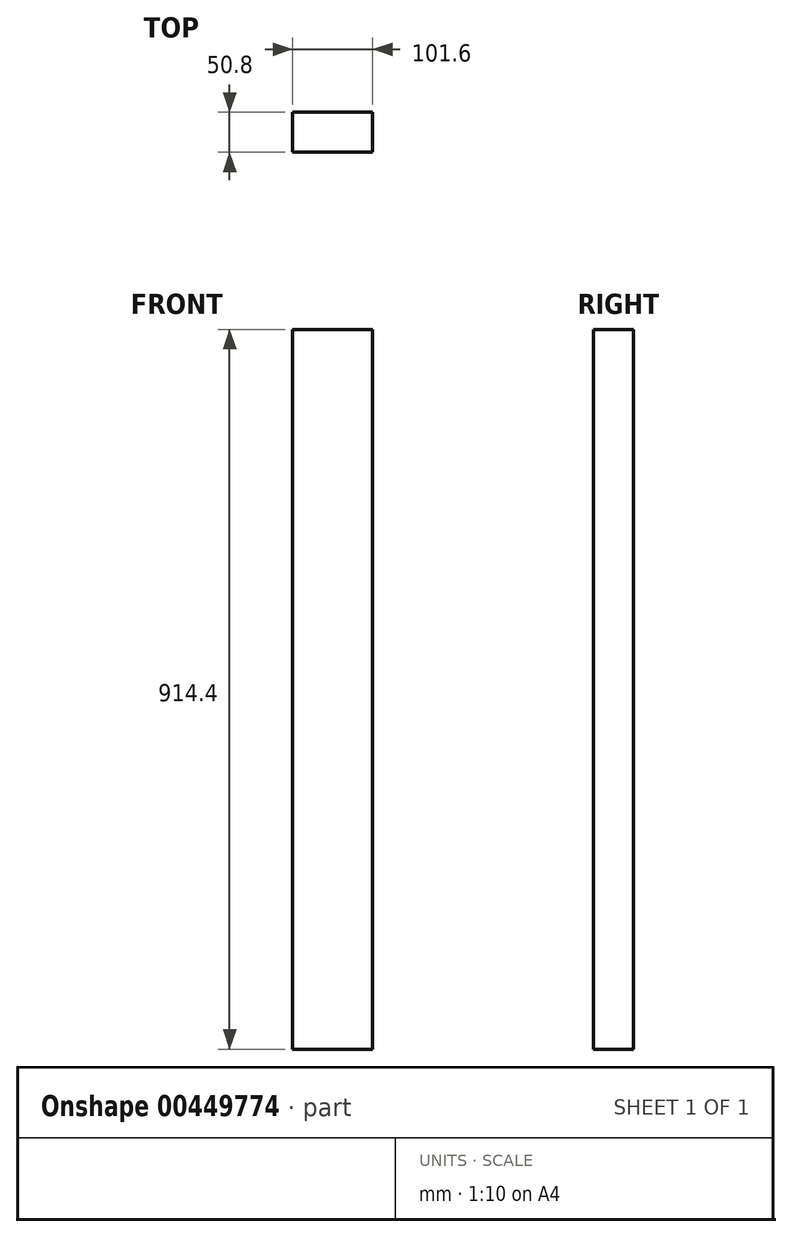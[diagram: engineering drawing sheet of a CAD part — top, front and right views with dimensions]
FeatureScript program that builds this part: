
annotation { "Feature Type Name" : "Feature", "Feature Type Description" : "" }
export const myFeature = defineFeature(function(context is Context, id is Id, definition is map)
    precondition{}
    {
        {
            var Q0;
            Q0=qCreatedBy(makeId("Front.planeOp"),FACE);
            var sketch = newSketch(context, id + "F0", { "sketchPlane" : qUnion([Q0])});
            skLineSegment(sketch, "E0", {"start": v(-59.95, 870.76) * mm, "end": v(-59.95, -43.64) * mm});
            skLineSegment(sketch, "E1", {"start": v(-59.95, -43.64) * mm, "end": v(41.65, -43.64) * mm});
            skLineSegment(sketch, "E2", {"start": v(41.65, -43.64) * mm, "end": v(41.65, 870.76) * mm});
            skLineSegment(sketch, "E3", {"start": v(41.65, 870.76) * mm, "end": v(-59.95, 870.76) * mm});
            skSolve(sketch);
        }
        {
            var Q0;
            Q0=makeQuery(id+"F0.imprint","IMPRINT",FACE,{"disambiguationData":[TD([[makeQuery(id+"F0.imprint","IMPRINT",EDGE,{"derivedFrom":sQuery(id+"F0.wireOp",EDGE,"E0")}),1.0]])]});
            extrude(context, id + "F1", {"entities" : qUnion([Q0]), "depth" : 50.8 * mm});
        }
    });
